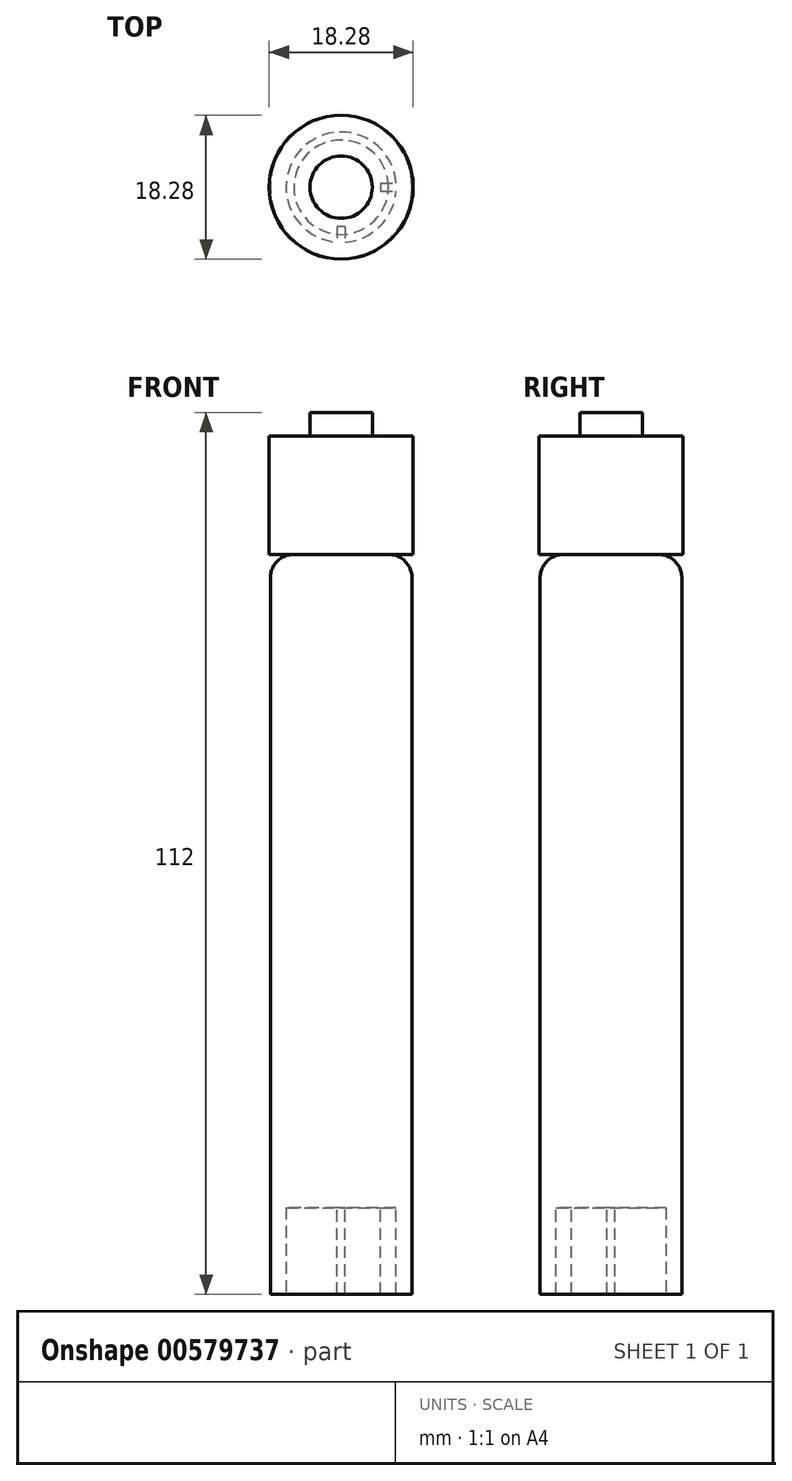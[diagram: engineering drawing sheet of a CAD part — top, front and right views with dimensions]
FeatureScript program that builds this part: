
annotation { "Feature Type Name" : "Feature", "Feature Type Description" : "" }
export const myFeature = defineFeature(function(context is Context, id is Id, definition is map)
    precondition{}
    {
        {
            var Q0;
            Q0=qCreatedBy(makeId("Front.planeOp"),FACE);
            var sketch = newSketch(context, id + "F0", { "sketchPlane" : qUnion([Q0])});
            skLineSegment(sketch, "E0", {"start": v(0, 0) * mm, "end": v(9, 0) * mm});
            skLineSegment(sketch, "E1", {"start": v(9, 0) * mm, "end": v(9, 89) * mm});
            skLineSegment(sketch, "E2", {"start": v(9, 89) * mm, "end": v(0, 89) * mm});
            skLineSegment(sketch, "E3", {"start": v(0, 89) * mm, "end": v(0, 0) * mm});
            skSolve(sketch);
        }
        {
            var Q0;
            Q0=makeQuery(id+"F0.imprint","IMPRINT",FACE,{"disambiguationData":[TD([[makeQuery(id+"F0.imprint","IMPRINT",EDGE,{"derivedFrom":sQuery(id+"F0.wireOp",EDGE,"E0")}),1.0]])]});
            var Q1;
            Q1=sQuery(id+"F0.wireOp",EDGE,"E3");
            revolve(context, id + "F1", {"entities" : qUnion([Q0]), "axis" : qUnion([Q1]), "revolveType" : RevolveType.FULL});
        }
        {
            var Q0;
            Q0=makeQuery(id+"F1.opRevolve","SWEPT_FACE",FACE,{"disambiguationData":[OSD([sQuery(id+"F0.wireOp",EDGE,"E2")])]});
            var sketch = newSketch(context, id + "F2", { "sketchPlane" : qUnion([Q0])});
            skCircle(sketch, "E4", {"center": v(0, 0) * mm, "radius": 9 * mm});
            skSolve(sketch);
        }
        {
            var Q0;
            Q0=makeQuery(id+"F2.imprint","IMPRINT",FACE,{"disambiguationData":[TD([[makeQuery(id+"F2.imprint","IMPRINT",EDGE,{"derivedFrom":sQuery(id+"F2.wireOp",EDGE,"E4")}),1.0]])]});
            extrude(context, id + "F3", {"entities" : qUnion([Q0]), "operationType" : NewBodyOperationType.ADD, "depth" : 5 * mm, "offsetDistance" : 25 * mm});
        }
        {
            var Q0;
            Q0=makeQuery(id+"F3.opExtrude","CAP_EDGE",EDGE,{"disambiguationData":[OSD([sQuery(id+"F2.wireOp",EDGE,"E4")])],"isStart":false});
            fillet(context, id + "F4", {"entities" : qUnion([Q0]), "radius" : 3 * mm, "tangentPropagation" : true, "allowEdgeOverflow" : false});
        }
        {
            var Q0;
            Q0=makeQuery(id+"F1.opRevolve","SWEPT_FACE",FACE,{"disambiguationData":[OSD([sQuery(id+"F0.wireOp",EDGE,"E0")])]});
            var sketch = newSketch(context, id + "F5", { "sketchPlane" : qUnion([Q0])});
            skCircle(sketch, "E5", {"center": v(0, 0) * mm, "radius": 7 * mm});
            skSolve(sketch);
        }
        {
            var Q0;
            Q0=makeQuery(id+"F5.imprint","IMPRINT",FACE,{"disambiguationData":[TD([[makeQuery(id+"F5.imprint","IMPRINT",EDGE,{"derivedFrom":sQuery(id+"F5.wireOp",EDGE,"E5")}),1.0]])]});
            extrude(context, id + "F6", {"entities" : qUnion([Q0]), "operationType" : NewBodyOperationType.REMOVE, "oppositeDirection" : true, "depth" : 11 * mm, "offsetDistance" : 25 * mm});
        }
        {
            var Q0;
            Q0=makeQuery(id+"F6.boolean.opBoolean","COPY",FACE,{"derivedFrom":makeQuery(id+"F6.opExtrude","CAP_FACE",FACE,{"disambiguationData":[OSD([sQuery(id+"F5.wireOp",EDGE,"E5")])],"isStart":false})});
            var sketch = newSketch(context, id + "F7", { "sketchPlane" : qUnion([Q0])});
            skLineSegment(sketch, "E6", {"start": v(0, 5) * mm, "end": v(0.5, 5) * mm});
            skLineSegment(sketch, "E7", {"start": v(0, 5) * mm, "end": v(-0.5, 5) * mm});
            skLineSegment(sketch, "E8", {"start": v(-0.5, 5) * mm, "end": v(-0.5, 6.98) * mm});
            skLineSegment(sketch, "E9", {"start": v(-0.5, 6.98) * mm, "end": v(-0.5, 5) * mm});
            skLineSegment(sketch, "E10", {"start": v(0.5, 5) * mm, "end": v(0.5, 6.98) * mm});
            skLineSegment(sketch, "E11", {"start": v(5, 0) * mm, "end": v(5, -0.5) * mm});
            skLineSegment(sketch, "E12", {"start": v(5, -0.5) * mm, "end": v(5, 0.5) * mm});
            skLineSegment(sketch, "E13", {"start": v(5, 0.5) * mm, "end": v(7, 0.5) * mm});
            skLineSegment(sketch, "E14", {"start": v(7, 0.5) * mm, "end": v(5, 0.5) * mm});
            skLineSegment(sketch, "E15", {"start": v(5, -0.5) * mm, "end": v(7, -0.5) * mm});
            skLineSegment(sketch, "E16", {"start": v(0, -5) * mm, "end": v(0.5, -5) * mm});
            skLineSegment(sketch, "E17", {"start": v(0.5, -5) * mm, "end": v(-0.5, -5) * mm});
            skLineSegment(sketch, "E18", {"start": v(-0.5, -5) * mm, "end": v(-0.5, -6.98) * mm});
            skLineSegment(sketch, "E19", {"start": v(-0.5, -6.98) * mm, "end": v(-0.5, -5) * mm});
            skLineSegment(sketch, "E20", {"start": v(0.5, -5) * mm, "end": v(0.5, -6.98) * mm});
            skLineSegment(sketch, "E21", {"start": v(-5, 0) * mm, "end": v(-5, 0.5) * mm});
            skLineSegment(sketch, "E22", {"start": v(-5, 0.5) * mm, "end": v(-5, -0.5) * mm});
            skLineSegment(sketch, "E23", {"start": v(-5, -0.5) * mm, "end": v(-6.98, -0.5) * mm});
            skLineSegment(sketch, "E24", {"start": v(-6.98, -0.5) * mm, "end": v(-5, -0.5) * mm});
            skLineSegment(sketch, "E25", {"start": v(-5, 0.5) * mm, "end": v(-6.98, 0.5) * mm});
            skSolve(sketch);
        }
        {
            var Q0;
            {var subQ1=sQuery(id+"F7.wireOp",EDGE,"E24");Q0=makeQuery(id+"F7.imprint","IMPRINT",FACE,{"disambiguationData":[TD([[makeQuery(id+"F7.imprint","IMPRINT",EDGE,{"derivedFrom":subQ1}),1.0]])]});}
            var Q1;
            Q1=makeQuery(id+"F7.imprint","IMPRINT",FACE,{"disambiguationData":[TD([[makeQuery(id+"F7.imprint","IMPRINT",EDGE,{"derivedFrom":sQuery(id+"F7.wireOp",EDGE,"E6")}),1.0]])]});
            var Q2;
            {var subQ1=sQuery(id+"F7.wireOp",EDGE,"E12");var subQ8=makeQuery(id+"F7.imprint","IMPRINT",VERTEX,{"derivedFrom":subQ1});Q2=makeQuery(id+"F7.imprint","IMPRINT",FACE,{"disambiguationData":[TD([[makeQuery(id+"F7.imprint","IMPRINT",EDGE,{"disambiguationData":[TD([[subQ8,1.0]])],"derivedFrom":subQ1}),-1.0]])]});}
            var Q3;
            {var subQ1=sQuery(id+"F7.wireOp",EDGE,"E19");Q3=makeQuery(id+"F7.imprint","IMPRINT",FACE,{"disambiguationData":[TD([[makeQuery(id+"F7.imprint","IMPRINT",EDGE,{"derivedFrom":subQ1}),-1.0]])]});}
            extrude(context, id + "F8", {"entities" : qUnion([Q0, Q1, Q2, Q3]), "operationType" : NewBodyOperationType.ADD, "depth" : 11 * mm, "offsetDistance" : 25 * mm});
        }
        {
            var Q0;
            Q0=makeQuery(id+"F3.opExtrude","CAP_FACE",FACE,{"disambiguationData":[OSD([sQuery(id+"F2.wireOp",EDGE,"E4")])],"isStart":false});
            var sketch = newSketch(context, id + "F9", { "sketchPlane" : qUnion([Q0])});
            skCircle(sketch, "E26", {"center": v(0, 0) * mm, "radius": 9.14 * mm});
            skSolve(sketch);
        }
        {
            var Q0;
            Q0=makeQuery(id+"F9.imprint","IMPRINT",FACE,{"disambiguationData":[TD([[makeQuery(id+"F9.imprint","IMPRINT",EDGE,{"derivedFrom":sQuery(id+"F9.wireOp",EDGE,"E26")}),1.0]])]});
            var sketch = newSketch(context, id + "F10", { "sketchPlane" : qUnion([Q0])});
            skCircle(sketch, "E27", {"center": v(0, 0) * mm, "radius": 3.96 * mm});
            skSolve(sketch);
        }
        {
            var Q0;
            Q0 = qSketchRegion(id + "F10", true);
            extrude(context, id + "F11", {"entities" : qUnion([Q0]), "operationType" : NewBodyOperationType.ADD, "depth" : 18 * mm, "offsetDistance" : 25 * mm});
        }
        {
            var Q0;
            Q0 = qSketchRegion(id + "F9", true);
            extrude(context, id + "F12", {"entities" : qUnion([Q0]), "operationType" : NewBodyOperationType.ADD, "depth" : 15 * mm, "offsetDistance" : 25 * mm});
        }
    });
